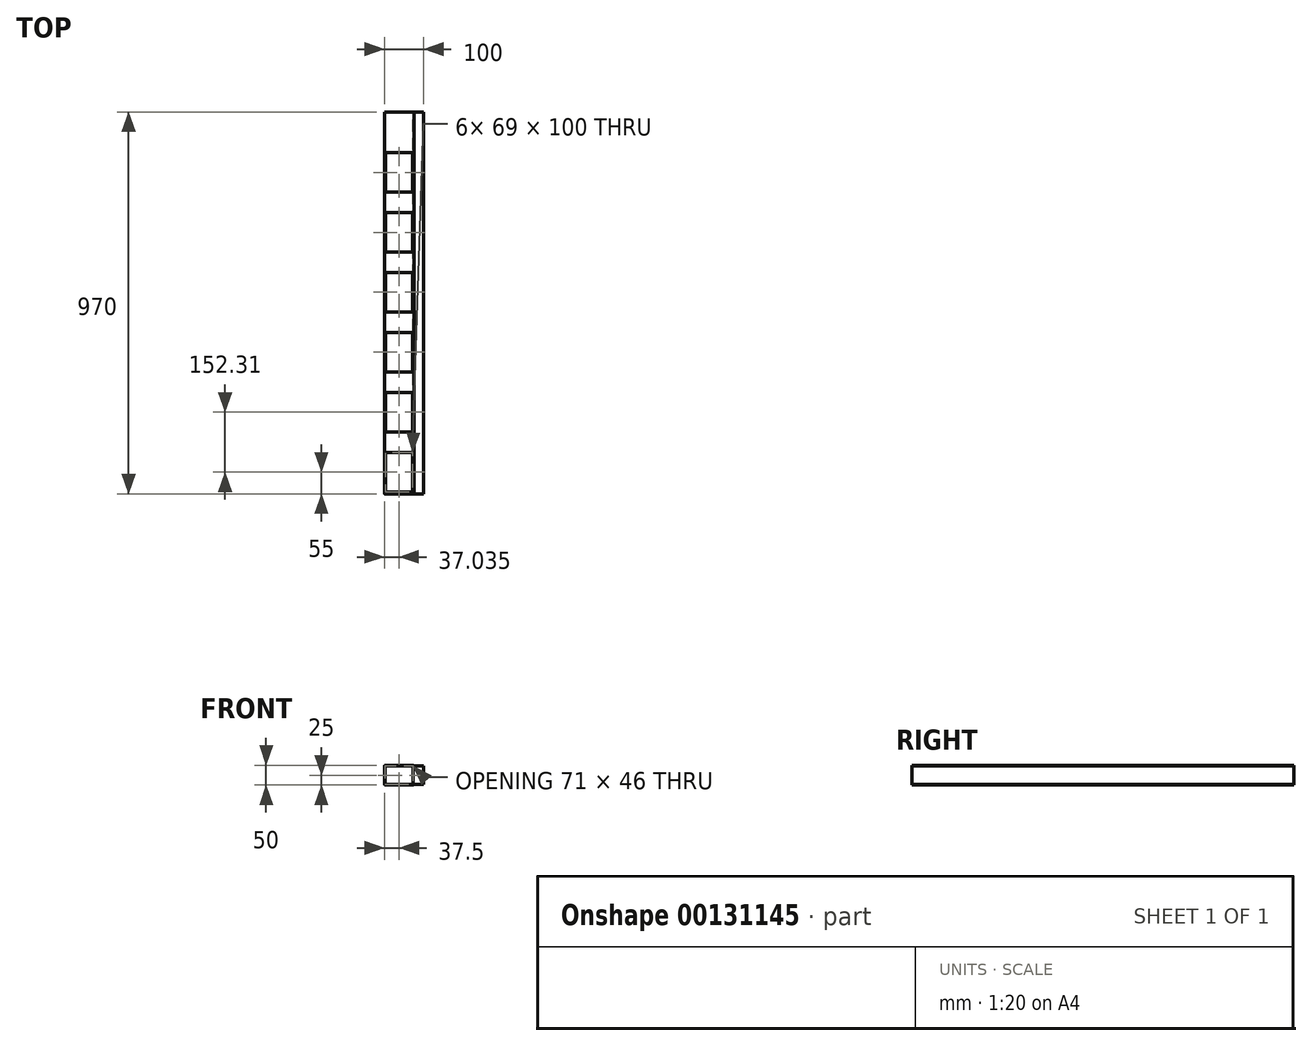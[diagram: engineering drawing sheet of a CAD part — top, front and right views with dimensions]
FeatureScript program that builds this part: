
annotation { "Feature Type Name" : "Feature", "Feature Type Description" : "" }
export const myFeature = defineFeature(function(context is Context, id is Id, definition is map)
    precondition{}
    {
        {
            var Q0;
            Q0=qCreatedBy(makeId("Front.planeOp"),FACE);
            var sketch = newSketch(context, id + "F0", { "sketchPlane" : qUnion([Q0])});
            skLineSegment(sketch, "E0.bottom", {"start": v(37.5, -25) * mm, "end": v(-37.5, -25) * mm});
            skLineSegment(sketch, "E0.top", {"start": v(37.5, 25) * mm, "end": v(-37.5, 25) * mm});
            skLineSegment(sketch, "E0.left", {"start": v(37.5, -25) * mm, "end": v(37.5, 25) * mm});
            skLineSegment(sketch, "E0.right", {"start": v(-37.5, -25) * mm, "end": v(-37.5, 25) * mm});
            skPoint(sketch, "E0.middle", {"position": v(0, 0) * mm});
            skLineSegment(sketch, "E1.bottom", {"start": v(35.5, -23) * mm, "end": v(-35.5, -23) * mm});
            skLineSegment(sketch, "E1.top", {"start": v(35.5, 23) * mm, "end": v(-35.5, 23) * mm});
            skLineSegment(sketch, "E1.left", {"start": v(35.5, -23) * mm, "end": v(35.5, 23) * mm});
            skLineSegment(sketch, "E1.right", {"start": v(-35.5, -23) * mm, "end": v(-35.5, 23) * mm});
            skSolve(sketch);
        }
        {
            var Q0;
            Q0=makeQuery(id+"F0.imprint","IMPRINT",FACE,{"disambiguationData":[TD([[makeQuery(id+"F0.imprint","IMPRINT",EDGE,{"derivedFrom":sQuery(id+"F0.wireOp",EDGE,"E0.bottom")}),-1.0]])]});
            extrude(context, id + "F1", {"entities" : qUnion([Q0]), "depth" : 970 * mm});
        }
        {
            var Q0;
            Q0=makeQuery(id+"F1.opExtrude","SWEPT_FACE",FACE,{"disambiguationData":[OSD([sQuery(id+"F0.wireOp",EDGE,"E0.top")])]});
            var sketch = newSketch(context, id + "F2", { "sketchPlane" : qUnion([Q0])});
            skLineSegment(sketch, "E2.bottom", {"start": v(34.03, -965) * mm, "end": v(-34.97, -965) * mm});
            skLineSegment(sketch, "E2.top", {"start": v(34.03, -865) * mm, "end": v(-34.97, -865) * mm});
            skLineSegment(sketch, "E2.left", {"start": v(34.03, -965) * mm, "end": v(34.03, -865) * mm});
            skLineSegment(sketch, "E2.right", {"start": v(-34.97, -965) * mm, "end": v(-34.97, -865) * mm});
            skPoint(sketch, "E2.middle", {"position": v(0, -485) * mm});
            skPoint(sketch, "E2.middle.positionSnap0", {"position": v(-37.5, -485) * mm});
            skPoint(sketch, "E2.centerSnap0", {"position": v(-37.5, -485) * mm});
            skLineSegment(sketch, "E3.bottom", {"start": v(34.03, -812.7) * mm, "end": v(-34.97, -812.7) * mm});
            skLineSegment(sketch, "E3.top", {"start": v(34.03, -712.7) * mm, "end": v(-34.97, -712.7) * mm});
            skLineSegment(sketch, "E3.left", {"start": v(34.03, -812.7) * mm, "end": v(34.03, -712.7) * mm});
            skLineSegment(sketch, "E3.right", {"start": v(-34.97, -812.7) * mm, "end": v(-34.97, -712.7) * mm});
            skLineSegment(sketch, "E4.bottom", {"start": v(34.03, -660.38) * mm, "end": v(-34.97, -660.38) * mm});
            skLineSegment(sketch, "E4.top", {"start": v(34.03, -560.38) * mm, "end": v(-34.97, -560.38) * mm});
            skLineSegment(sketch, "E4.left", {"start": v(34.03, -660.38) * mm, "end": v(34.03, -560.38) * mm});
            skLineSegment(sketch, "E4.right", {"start": v(-34.97, -660.38) * mm, "end": v(-34.97, -560.38) * mm});
            skLineSegment(sketch, "E5.bottom", {"start": v(34.03, -508.07) * mm, "end": v(-34.97, -508.07) * mm});
            skLineSegment(sketch, "E5.top", {"start": v(34.03, -408.07) * mm, "end": v(-34.97, -408.07) * mm});
            skLineSegment(sketch, "E5.left", {"start": v(34.03, -508.07) * mm, "end": v(34.03, -408.07) * mm});
            skLineSegment(sketch, "E5.right", {"start": v(-34.97, -508.07) * mm, "end": v(-34.97, -408.07) * mm});
            skPoint(sketch, "E5.middle", {"position": v(0.05, -26.06) * mm});
            skPoint(sketch, "E5.middle.positionSnap0", {"position": v(-37.45, -26.06) * mm});
            skPoint(sketch, "E5.centerSnap0", {"position": v(-37.45, -26.06) * mm});
            skLineSegment(sketch, "E6.bottom", {"start": v(34.03, -355.76) * mm, "end": v(-34.97, -355.76) * mm});
            skLineSegment(sketch, "E6.top", {"start": v(34.03, -255.76) * mm, "end": v(-34.97, -255.76) * mm});
            skLineSegment(sketch, "E6.left", {"start": v(34.03, -355.76) * mm, "end": v(34.03, -255.76) * mm});
            skLineSegment(sketch, "E6.right", {"start": v(-34.97, -355.76) * mm, "end": v(-34.97, -255.76) * mm});
            skLineSegment(sketch, "E7.bottom", {"start": v(34.03, -203.45) * mm, "end": v(-34.97, -203.45) * mm});
            skLineSegment(sketch, "E7.top", {"start": v(34.03, -103.45) * mm, "end": v(-34.97, -103.45) * mm});
            skLineSegment(sketch, "E7.left", {"start": v(34.03, -203.45) * mm, "end": v(34.03, -103.45) * mm});
            skLineSegment(sketch, "E7.right", {"start": v(-34.97, -203.45) * mm, "end": v(-34.97, -103.45) * mm});
            skSolve(sketch);
        }
        {
            var Q0;
            Q0=makeQuery(id+"F1.opExtrude","SWEPT_EDGE",EDGE,{"disambiguationData":[OSD([sQuery(id+"F0.wireOp",EDGE,"E0.top"),sQuery(id+"F0.wireOp",EDGE,"E0.right")])]});
            var Q1;
            Q1=makeQuery(id+"F1.opExtrude","SWEPT_EDGE",EDGE,{"disambiguationData":[OSD([sQuery(id+"F0.wireOp",EDGE,"E0.top"),sQuery(id+"F0.wireOp",EDGE,"E0.left")])]});
            var Q2;
            Q2=makeQuery(id+"F1.opExtrude","SWEPT_EDGE",EDGE,{"disambiguationData":[OSD([sQuery(id+"F0.wireOp",EDGE,"E0.bottom"),sQuery(id+"F0.wireOp",EDGE,"E0.left")])]});
            var Q3;
            Q3=makeQuery(id+"F1.opExtrude","SWEPT_EDGE",EDGE,{"disambiguationData":[OSD([sQuery(id+"F0.wireOp",EDGE,"E0.bottom"),sQuery(id+"F0.wireOp",EDGE,"E0.right")])]});
            fillet(context, id + "F3", {"entities" : qUnion([Q0, Q1, Q2, Q3]), "radius" : 2 * mm, "tangentPropagation" : true, "allowEdgeOverflow" : false});
        }
        {
            var Q0;
            Q0=makeQuery(id+"F1.opExtrude","SWEPT_EDGE",EDGE,{"disambiguationData":[OSD([sQuery(id+"F0.wireOp",EDGE,"E1.top"),sQuery(id+"F0.wireOp",EDGE,"E1.right")])]});
            var Q1;
            Q1=makeQuery(id+"F1.opExtrude","SWEPT_EDGE",EDGE,{"disambiguationData":[OSD([sQuery(id+"F0.wireOp",EDGE,"E1.bottom"),sQuery(id+"F0.wireOp",EDGE,"E1.right")])]});
            var Q2;
            Q2=makeQuery(id+"F1.opExtrude","SWEPT_EDGE",EDGE,{"disambiguationData":[OSD([sQuery(id+"F0.wireOp",EDGE,"E1.bottom"),sQuery(id+"F0.wireOp",EDGE,"E1.left")])]});
            var Q3;
            Q3=makeQuery(id+"F1.opExtrude","SWEPT_EDGE",EDGE,{"disambiguationData":[OSD([sQuery(id+"F0.wireOp",EDGE,"E1.top"),sQuery(id+"F0.wireOp",EDGE,"E1.left")])]});
            fillet(context, id + "F4", {"entities" : qUnion([Q0, Q1, Q2, Q3]), "radius" : 2 * mm, "tangentPropagation" : true, "allowEdgeOverflow" : false});
        }
        {
            var Q0;
            Q0 = qSketchRegion(id + "F2", true);
            extrude(context, id + "F5", {"entities" : qUnion([Q0]), "operationType" : NewBodyOperationType.REMOVE, "oppositeDirection" : true, "depth" : 60 * mm});
        }
        {
            var Q0;
            Q0=makeQuery(id+"F1.opExtrude","SWEPT_FACE",FACE,{"disambiguationData":[OSD([sQuery(id+"F0.wireOp",EDGE,"E0.left")])]});
            extrude(context, id + "F6", {"entities" : qUnion([Q0]), "operationType" : NewBodyOperationType.ADD, "depth" : 25 * mm});
        }
    });
